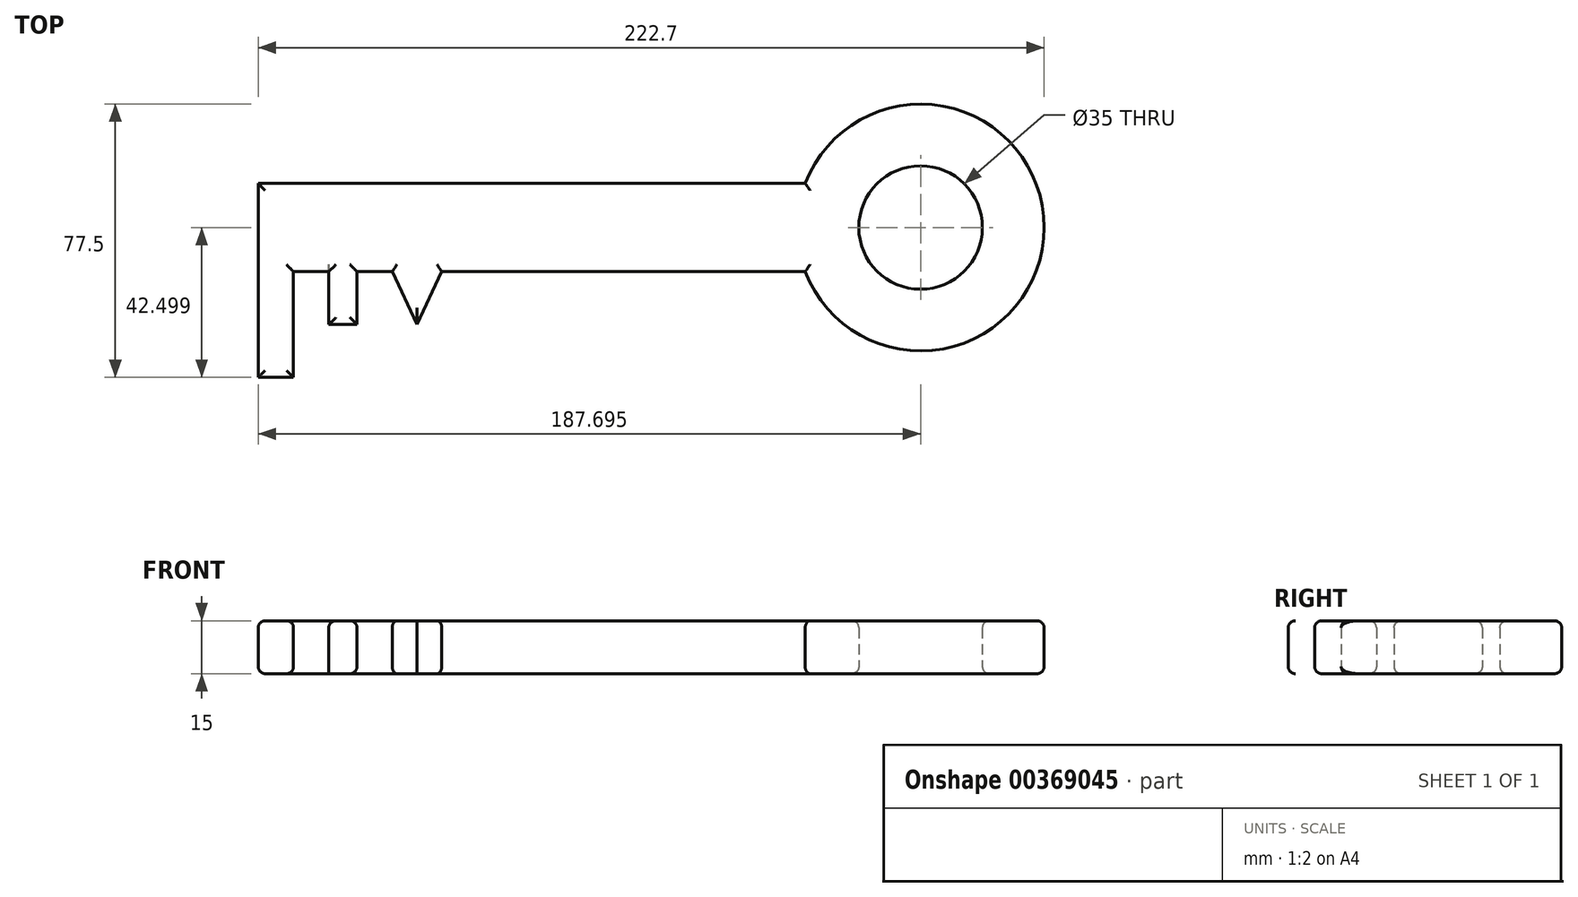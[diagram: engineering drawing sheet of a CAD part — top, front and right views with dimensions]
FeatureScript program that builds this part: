
annotation { "Feature Type Name" : "Feature", "Feature Type Description" : "" }
export const myFeature = defineFeature(function(context is Context, id is Id, definition is map)
    precondition{}
    {
        {
            var Q0;
            Q0=qCreatedBy(makeId("Top.planeOp"),FACE);
            var sketch = newSketch(context, id + "F0", { "sketchPlane" : qUnion([Q0])});
            skLineSegment(sketch, "E0.bottom", {"start": v(-117.55, 21.79) * mm, "end": v(37.45, 21.79) * mm});
            skLineSegment(sketch, "E0.top", {"start": v(-117.55, -3.21) * mm, "end": v(37.45, -3.21) * mm});
            skLineSegment(sketch, "E0.left", {"start": v(-117.55, 21.79) * mm, "end": v(-117.55, -3.21) * mm});
            skLineSegment(sketch, "E1.bottom", {"start": v(-117.55, -3.21) * mm, "end": v(-107.55, -3.21) * mm});
            skLineSegment(sketch, "E1.top", {"start": v(-117.55, -33.21) * mm, "end": v(-107.55, -33.21) * mm});
            skLineSegment(sketch, "E1.left", {"start": v(-117.55, -3.21) * mm, "end": v(-117.55, -33.21) * mm});
            skLineSegment(sketch, "E1.right", {"start": v(-107.55, -3.21) * mm, "end": v(-107.55, -33.21) * mm});
            skLineSegment(sketch, "E2.bottom", {"start": v(-97.55, -3.21) * mm, "end": v(-89.55, -3.21) * mm});
            skLineSegment(sketch, "E2.top", {"start": v(-97.55, -18.21) * mm, "end": v(-89.55, -18.21) * mm});
            skLineSegment(sketch, "E2.left", {"start": v(-97.55, -3.21) * mm, "end": v(-97.55, -18.21) * mm});
            skLineSegment(sketch, "E2.right", {"start": v(-89.55, -3.21) * mm, "end": v(-89.55, -18.21) * mm});
            skLineSegment(sketch, "E3", {"start": v(-79.55, -3.21) * mm, "end": v(-72.55, -18.21) * mm});
            skLineSegment(sketch, "E4", {"start": v(-65.55, -3.21) * mm, "end": v(-72.55, -18.21) * mm});
            skLineSegment(sketch, "E5", {"start": v(-79.55, -3.21) * mm, "end": v(-65.55, -3.21) * mm});
            skArc(sketch, "E6", {"start": v(37.45, -3.21) * mm, "mid": v(105.15, 9.29) * mm, "end": v(37.45, 21.79) * mm});
            skCircle(sketch, "E7", {"center": v(70.15, 9.29) * mm, "radius": 17.5 * mm});
            skLineSegment(sketch, "E8", {"start": v(70.15, 9.29) * mm, "end": v(-117.55, 9.29) * mm, "construction": true});
            skSolve(sketch);
        }
        {
            var Q0;
            Q0 = qSketchRegion(id + "F0", true);
            extrude(context, id + "F1", {"entities" : qUnion([Q0]), "depth" : 15 * mm});
        }
        {
            var Q0;
            Q0=makeQuery(id+"F1.opExtrude","CAP_EDGE",EDGE,{"disambiguationData":[OSD([sQuery(id+"F0.wireOp",EDGE,"E0.bottom")])],"isStart":false});
            var Q1;
            Q1=makeQuery(id+"F1.opExtrude","CAP_EDGE",EDGE,{"disambiguationData":[OSD([sQuery(id+"F0.wireOp",EDGE,"E0.left"),sQuery(id+"F0.wireOp",EDGE,"E1.left")])],"isStart":false});
            var Q2;
            Q2=makeQuery(id+"F1.opExtrude","CAP_FACE",FACE,{"disambiguationData":[OSD([sQuery(id+"F0.wireOp",EDGE,"E0.bottom"),sQuery(id+"F0.wireOp",EDGE,"E0.top"),sQuery(id+"F0.wireOp",EDGE,"E0.left"),sQuery(id+"F0.wireOp",EDGE,"E1.top"),sQuery(id+"F0.wireOp",EDGE,"E1.left"),sQuery(id+"F0.wireOp",EDGE,"E1.right"),sQuery(id+"F0.wireOp",EDGE,"E2.top"),sQuery(id+"F0.wireOp",EDGE,"E2.left"),sQuery(id+"F0.wireOp",EDGE,"E2.right"),sQuery(id+"F0.wireOp",EDGE,"E3"),sQuery(id+"F0.wireOp",EDGE,"E4"),sQuery(id+"F0.wireOp",EDGE,"E6"),sQuery(id+"F0.wireOp",EDGE,"E7")])],"isStart":false});
            var Q3;
            Q3=makeQuery(id+"F1.opExtrude","CAP_EDGE",EDGE,{"disambiguationData":[OSD([sQuery(id+"F0.wireOp",EDGE,"E1.right")])],"isStart":false});
            var Q4;
            Q4=makeQuery(id+"F1.opExtrude","CAP_EDGE",EDGE,{"disambiguationData":[OSD([sQuery(id+"F0.wireOp",EDGE,"E7")])],"isStart":false});
            var Q5;
            Q5=makeQuery(id+"F1.opExtrude","CAP_EDGE",EDGE,{"disambiguationData":[OSD([sQuery(id+"F0.wireOp",EDGE,"E6")])],"isStart":false});
            var Q6;
            {var subQ0=sQuery(id+"F0.wireOp",EDGE,"E0.top");Q6=makeQuery(id+"F1.opExtrude","CAP_EDGE",EDGE,{"disambiguationData":[OSD([subQ0]),TDD([makeQuery(id+"F0.imprint","IMPRINT",EDGE,{"disambiguationData":[TD([[makeQuery(id+"F0.imprint","INTERSECT",VERTEX,{"derivedFrom":[subQ0,sQuery(id+"F0.wireOp",EDGE,"E6")]}),1.0]])],"derivedFrom":subQ0})])],"isStart":false});}
            var Q7;
            Q7=makeQuery(id+"F1.opExtrude","CAP_EDGE",EDGE,{"disambiguationData":[OSD([sQuery(id+"F0.wireOp",EDGE,"E4")])],"isStart":false});
            var Q8;
            {var subQ0=sQuery(id+"F0.wireOp",EDGE,"E0.top");Q8=makeQuery(id+"F1.opExtrude","CAP_EDGE",EDGE,{"disambiguationData":[OSD([subQ0]),TDD([makeQuery(id+"F0.imprint","IMPRINT",EDGE,{"disambiguationData":[TD([[makeQuery(id+"F0.imprint","INTERSECT",VERTEX,{"derivedFrom":[subQ0,sQuery(id+"F0.wireOp",EDGE,"E2.bottom"),sQuery(id+"F0.wireOp",EDGE,"E2.right")]}),-1.0]])],"derivedFrom":subQ0})])],"isStart":false});}
            var Q9;
            Q9=makeQuery(id+"F1.opExtrude","CAP_EDGE",EDGE,{"disambiguationData":[OSD([sQuery(id+"F0.wireOp",EDGE,"E2.right")])],"isStart":false});
            var Q10;
            Q10=makeQuery(id+"F1.opExtrude","CAP_EDGE",EDGE,{"disambiguationData":[OSD([sQuery(id+"F0.wireOp",EDGE,"E2.top")])],"isStart":false});
            var Q11;
            Q11=makeQuery(id+"F1.opExtrude","CAP_EDGE",EDGE,{"disambiguationData":[OSD([sQuery(id+"F0.wireOp",EDGE,"E3")])],"isStart":false});
            var Q12;
            Q12=makeQuery(id+"F1.opExtrude","CAP_EDGE",EDGE,{"disambiguationData":[OSD([sQuery(id+"F0.wireOp",EDGE,"E2.left")])],"isStart":false});
            fillet(context, id + "F2", {"entities" : qUnion([Q0, Q1, Q2, Q3, Q4, Q5, Q6, Q7, Q8, Q9, Q10, Q11, Q12]), "radius" : 2 * mm, "tangentPropagation" : true, "allowEdgeOverflow" : false});
        }
        {
            var Q0;
            Q0=makeQuery(id+"F1.opExtrude","CAP_EDGE",EDGE,{"disambiguationData":[OSD([sQuery(id+"F0.wireOp",EDGE,"E6")])],"isStart":true});
            var Q1;
            Q1=makeQuery(id+"F1.opExtrude","CAP_EDGE",EDGE,{"disambiguationData":[OSD([sQuery(id+"F0.wireOp",EDGE,"E7")])],"isStart":true});
            var Q2;
            Q2=makeQuery(id+"F1.opExtrude","CAP_EDGE",EDGE,{"disambiguationData":[OSD([sQuery(id+"F0.wireOp",EDGE,"E0.bottom")])],"isStart":true});
            var Q3;
            {var subQ0=sQuery(id+"F0.wireOp",EDGE,"E0.top");Q3=makeQuery(id+"F1.opExtrude","CAP_EDGE",EDGE,{"disambiguationData":[OSD([subQ0]),TDD([makeQuery(id+"F0.imprint","IMPRINT",EDGE,{"disambiguationData":[TD([[makeQuery(id+"F0.imprint","INTERSECT",VERTEX,{"derivedFrom":[subQ0,sQuery(id+"F0.wireOp",EDGE,"E6")]}),1.0]])],"derivedFrom":subQ0})])],"isStart":true});}
            var Q4;
            Q4=makeQuery(id+"F1.opExtrude","CAP_EDGE",EDGE,{"disambiguationData":[OSD([sQuery(id+"F0.wireOp",EDGE,"E4")])],"isStart":true});
            var Q5;
            Q5=makeQuery(id+"F1.opExtrude","CAP_EDGE",EDGE,{"disambiguationData":[OSD([sQuery(id+"F0.wireOp",EDGE,"E2.right")])],"isStart":true});
            var Q6;
            Q6=makeQuery(id+"F1.opExtrude","CAP_EDGE",EDGE,{"disambiguationData":[OSD([sQuery(id+"F0.wireOp",EDGE,"E2.top")])],"isStart":true});
            var Q7;
            Q7=makeQuery(id+"F1.opExtrude","CAP_EDGE",EDGE,{"disambiguationData":[OSD([sQuery(id+"F0.wireOp",EDGE,"E1.right")])],"isStart":true});
            var Q8;
            Q8=makeQuery(id+"F1.opExtrude","CAP_EDGE",EDGE,{"disambiguationData":[OSD([sQuery(id+"F0.wireOp",EDGE,"E0.left"),sQuery(id+"F0.wireOp",EDGE,"E1.left")])],"isStart":true});
            var Q9;
            Q9=makeQuery(id+"F1.opExtrude","CAP_EDGE",EDGE,{"disambiguationData":[OSD([sQuery(id+"F0.wireOp",EDGE,"E1.top")])],"isStart":true});
            var Q10;
            {var subQ0=sQuery(id+"F0.wireOp",EDGE,"E0.top");Q10=makeQuery(id+"F1.opExtrude","CAP_EDGE",EDGE,{"disambiguationData":[OSD([subQ0]),TDD([makeQuery(id+"F0.imprint","IMPRINT",EDGE,{"disambiguationData":[TD([[makeQuery(id+"F0.imprint","INTERSECT",VERTEX,{"derivedFrom":[subQ0,sQuery(id+"F0.wireOp",EDGE,"E1.bottom"),sQuery(id+"F0.wireOp",EDGE,"E1.right")]}),-1.0]])],"derivedFrom":subQ0})])],"isStart":true});}
            var Q11;
            {var subQ0=sQuery(id+"F0.wireOp",EDGE,"E0.top");Q11=makeQuery(id+"F1.opExtrude","CAP_EDGE",EDGE,{"disambiguationData":[OSD([subQ0]),TDD([makeQuery(id+"F0.imprint","IMPRINT",EDGE,{"disambiguationData":[TD([[makeQuery(id+"F0.imprint","INTERSECT",VERTEX,{"derivedFrom":[subQ0,sQuery(id+"F0.wireOp",EDGE,"E2.bottom"),sQuery(id+"F0.wireOp",EDGE,"E2.right")]}),-1.0]])],"derivedFrom":subQ0})])],"isStart":true});}
            var Q12;
            Q12=makeQuery(id+"F1.opExtrude","CAP_EDGE",EDGE,{"disambiguationData":[OSD([sQuery(id+"F0.wireOp",EDGE,"E3")])],"isStart":true});
            fillet(context, id + "F3", {"entities" : qUnion([Q0, Q1, Q2, Q3, Q4, Q5, Q6, Q7, Q8, Q9, Q10, Q11, Q12]), "radius" : 2 * mm, "tangentPropagation" : true, "allowEdgeOverflow" : false});
        }
    });
